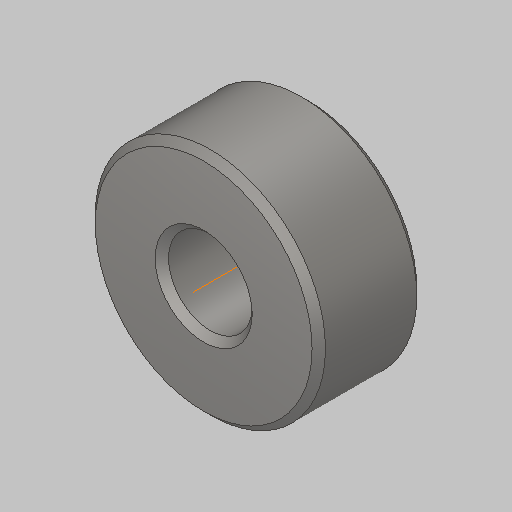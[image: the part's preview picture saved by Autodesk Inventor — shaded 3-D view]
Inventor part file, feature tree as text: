
AUTODESK INVENTOR PART (.ipt)
format: ipt  version: 2023.5 (Build 275446000, 446)  size: 130,048 bytes
history: native  units: in
note: dims shown in document units (in); Inventor stores cm internally (conversion verified against a paired STEP export)
features: plane x2, extrude x1, chamfer x1
ambient origin geometry x8: Origin, YZ Plane, XZ Plane, XY Plane, X Axis, Y Axis, Z Axis, Center Point
bodies: Solid1 (feature_tree)
feature tree (4):
  extrude  "Extrusion1"  Depth=0.3125in TaperAngle=0.0deg
  chamfer  "Chamfer1"  Distance=0.125in Angle=45.0deg
  plane  "Work Plane1"
  plane  "Work Plane2"
